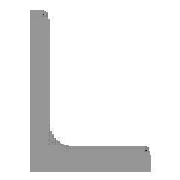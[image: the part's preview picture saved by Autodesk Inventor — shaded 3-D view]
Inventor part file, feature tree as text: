
AUTODESK INVENTOR PART (.ipt)
format: ipt  version: 2024.1 (Build 281209000, 209)  size: 132,608 bytes
history: native  units: mm (DEFAULTED — no unit token found)
features: other x4, plane x3, split x2, sketch x1
ambient origin geometry x8: Origin, YZ Plane, XZ Plane, XY Plane, X Axis, Y Axis, Z Axis, Center Point
bodies: Solid1 (feature_tree), Body (feature_tree)
feature tree (10):
  parser-record x1  (decoder bookkeeping rows leaked as tree rows — omitted from the tree; the rows remain in map.json)
  other  "Driven Length"
  other  "Start Plane"
  other  "End Plane"
  plane  "Work Plane4"
  split  "Split1"
  plane  "Work Plane5"
  split  "Split2"
  sketch  "Sketch3"  dims[d0=25.4mm d1=25.4mm d2=3.175mm d3=3.175mm d4=1025.4mm d5=0.0mm d10=0.0mm d11=0.0mm d12=-12.7mm d13=1012.7mm d14=3.302mm d15=1.524mm d16=90.0deg d17=1025.4mm]
  plane  "Work Plane3"
